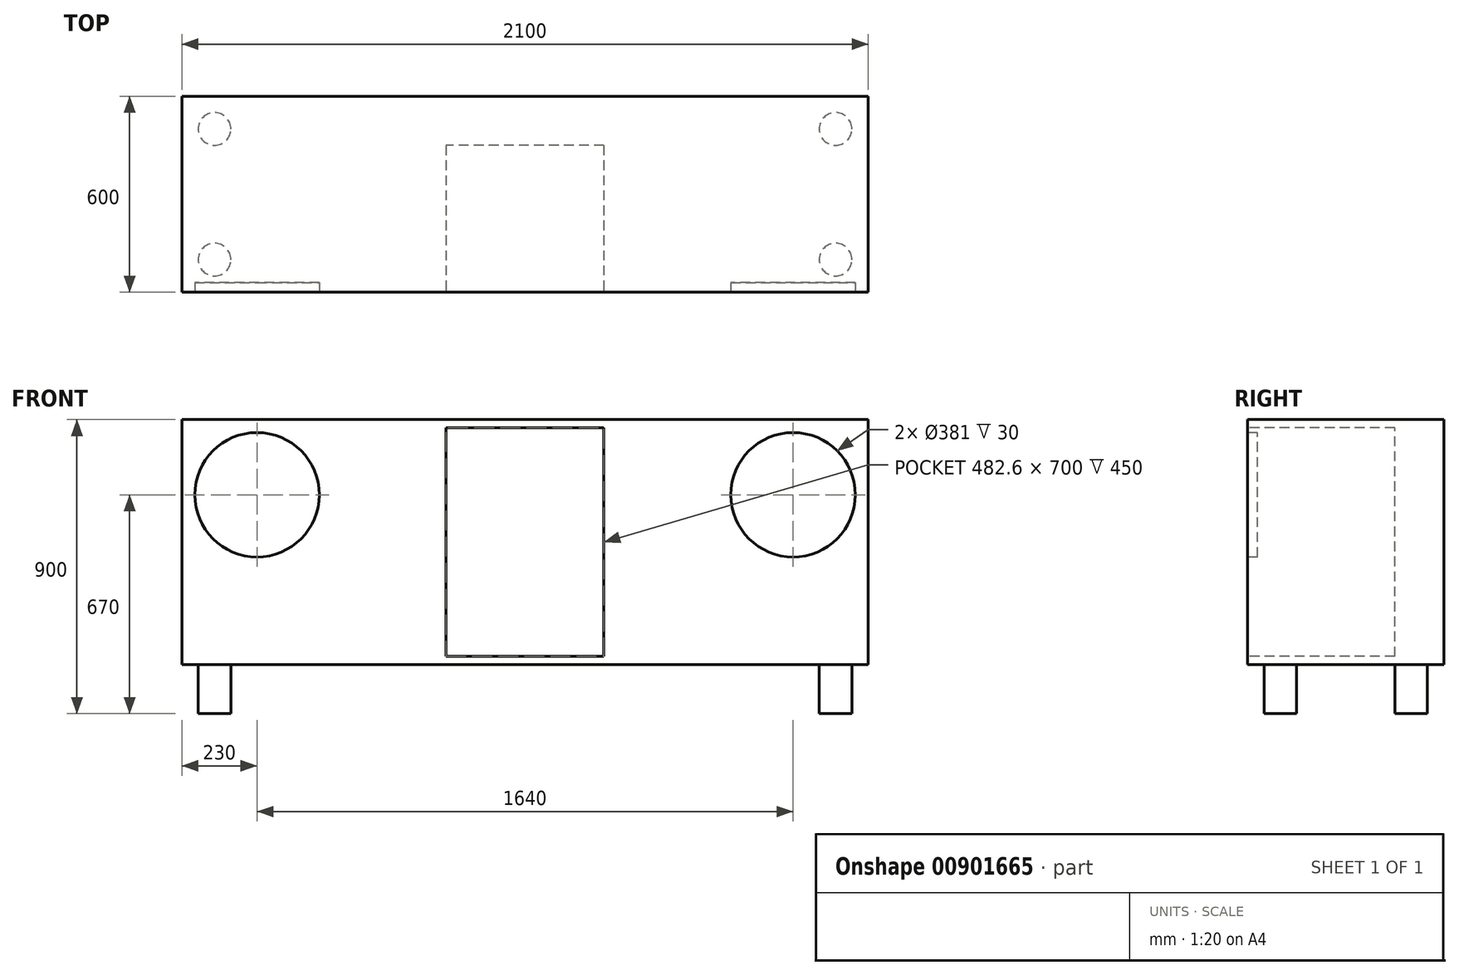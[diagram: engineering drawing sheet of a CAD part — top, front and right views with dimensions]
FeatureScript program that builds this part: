
annotation { "Feature Type Name" : "Feature", "Feature Type Description" : "" }
export const myFeature = defineFeature(function(context is Context, id is Id, definition is map)
    precondition{}
    {
        {
            var Q0;
            Q0=qCreatedBy(makeId("Front.planeOp"),FACE);
            var sketch = newSketch(context, id + "F0", { "sketchPlane" : qUnion([Q0])});
            skLineSegment(sketch, "E0.bottom", {"start": v(1050, -750) * mm, "end": v(-1050, -750) * mm});
            skLineSegment(sketch, "E0.top", {"start": v(1050, 0) * mm, "end": v(-1050, 0) * mm});
            skLineSegment(sketch, "E0.left", {"start": v(1050, -750) * mm, "end": v(1050, 0) * mm});
            skLineSegment(sketch, "E0.right", {"start": v(-1050, -750) * mm, "end": v(-1050, 0) * mm});
            skPoint(sketch, "E0.middle", {"position": v(0, -375) * mm});
            skSolve(sketch);
        }
        {
            var Q0;
            Q0 = qSketchRegion(id + "F0", true);
            extrude(context, id + "F1", {"entities" : qUnion([Q0]), "depth" : 600 * mm, "offsetDistance" : 25 * mm});
        }
        {
            var Q0;
            Q0=makeQuery(id+"F1.opExtrude","CAP_FACE",FACE,{"disambiguationData":[OSD([sQuery(id+"F0.wireOp",EDGE,"E0.bottom"),sQuery(id+"F0.wireOp",EDGE,"E0.top"),sQuery(id+"F0.wireOp",EDGE,"E0.left"),sQuery(id+"F0.wireOp",EDGE,"E0.right")])],"isStart":false});
            var sketch = newSketch(context, id + "F2", { "sketchPlane" : qUnion([Q0])});
            skLineSegment(sketch, "E1.bottom", {"start": v(241.3, -725) * mm, "end": v(-241.3, -725) * mm});
            skLineSegment(sketch, "E1.top", {"start": v(241.3, -25) * mm, "end": v(-241.3, -25) * mm});
            skLineSegment(sketch, "E1.left", {"start": v(241.3, -725) * mm, "end": v(241.3, -25) * mm});
            skLineSegment(sketch, "E1.right", {"start": v(-241.3, -725) * mm, "end": v(-241.3, -25) * mm});
            skPoint(sketch, "E1.middle", {"position": v(0, -375) * mm});
            skSolve(sketch);
        }
        {
            var Q0;
            Q0 = qSketchRegion(id + "F2", true);
            extrude(context, id + "F3", {"entities" : qUnion([Q0]), "operationType" : NewBodyOperationType.REMOVE, "oppositeDirection" : true, "depth" : 450 * mm, "offsetDistance" : 25 * mm});
        }
        {
            var Q0;
            Q0=makeQuery(id+"F1.opExtrude","SWEPT_FACE",FACE,{"disambiguationData":[OSD([sQuery(id+"F0.wireOp",EDGE,"E0.bottom")])]});
            var sketch = newSketch(context, id + "F4", { "sketchPlane" : qUnion([Q0])});
            skCircle(sketch, "E2", {"center": v(-950, 500) * mm, "radius": 50 * mm});
            skCircle(sketch, "E3", {"center": v(-950, 100) * mm, "radius": 50 * mm});
            skCircle(sketch, "E4", {"center": v(950, 100) * mm, "radius": 50 * mm});
            skCircle(sketch, "E5", {"center": v(950, 500) * mm, "radius": 50 * mm});
            skSolve(sketch);
        }
        {
            var Q0;
            Q0 = qSketchRegion(id + "F4", true);
            extrude(context, id + "F5", {"entities" : qUnion([Q0]), "depth" : 150 * mm, "offsetDistance" : 25 * mm});
        }
        {
            var Q0;
            Q0=makeQuery(id+"F1.opExtrude","CAP_FACE",FACE,{"disambiguationData":[OSD([sQuery(id+"F0.wireOp",EDGE,"E0.bottom"),sQuery(id+"F0.wireOp",EDGE,"E0.top"),sQuery(id+"F0.wireOp",EDGE,"E0.left"),sQuery(id+"F0.wireOp",EDGE,"E0.right")])],"isStart":false});
            var sketch = newSketch(context, id + "F6", { "sketchPlane" : qUnion([Q0])});
            skCircle(sketch, "E6", {"center": v(-820, -230) * mm, "radius": 190.5 * mm});
            skCircle(sketch, "E7", {"center": v(820, -230) * mm, "radius": 190.5 * mm});
            skSolve(sketch);
        }
        {
            var Q0;
            Q0 = qSketchRegion(id + "F6", true);
            extrude(context, id + "F7", {"entities" : qUnion([Q0]), "operationType" : NewBodyOperationType.REMOVE, "oppositeDirection" : true, "depth" : 30 * mm, "offsetDistance" : 25 * mm});
        }
    });
